FCSTD DOCUMENT  (FreeCAD 0.19R)
Label: EBLclip
License: All rights reserved
LicenseURL: http://en.wikipedia.org/wiki/All_rights_reserved
objects: PartDesign::Chamfer×8, Sketcher::SketchObject×4, PartDesign::Pocket×3, PartDesign::Fillet×2, PartDesign::Pad×1, PartDesign::Body×1, Mesh::Feature×1
note: 33 computed .brp shape members not serialized (recipe doc carries the construction recipe); baked Part::Feature solids carry a one-line shape summary decoded from their .brp

FEATURE [Sketcher::SketchObject] Sketch
  FullyConstrained = true
  MapMode = 5
  Placement = pos=(0,0,0) rot=(1,0,0;1.5708rad)
  Support = -> [XZ_Plane]
  sketch-geometry (8):
    g0: LineSegment StartX=-75 StartY=0 StartZ=0 EndX=-75 EndY=4 EndZ=0
    g1: LineSegment StartX=-75 StartY=4 StartZ=0 EndX=-65 EndY=4 EndZ=0
    g2: LineSegment StartX=-65 StartY=4 StartZ=0 EndX=-65 EndY=30 EndZ=0
    g3: LineSegment StartX=-65 StartY=30 StartZ=0 EndX=65 EndY=30 EndZ=0
    g4: LineSegment StartX=65 StartY=30 StartZ=0 EndX=65 EndY=4 EndZ=0
    g5: LineSegment StartX=65 StartY=4 StartZ=0 EndX=75 EndY=4 EndZ=0
    g6: LineSegment StartX=75 StartY=4 StartZ=0 EndX=75 EndY=0 EndZ=0
    g7: LineSegment StartX=75 StartY=0 StartZ=0 EndX=-75 EndY=0 EndZ=0
  constraints (21):
    c: PointOnObject(g0,g-1)
    c: Coincident(g0,g1)
    c: Horizontal(g1)
    c: Coincident(g2,g3)
    c: Coincident(g3,g4)
    c: Vertical(g4)
    c: Coincident(g5,g6)
    c: Coincident(g7,g0)
    c: Horizontal(g7)
    c: Symmetric(g3,g2,g-2)
    c: Symmetric(g1,g4,g-2)
    c: Coincident(g4,g5)
    c: Vertical(g0)
    c: Vertical(g6)
    c: Symmetric(g0,g5,g-2)
    c: Distance(g6) = 4
    c: Coincident(g2,g1)
    c: Distance(g5) = 10
    c: Coincident(g7,g6)
    c: Distance(g4,g1) = 130
    c: DistanceY(g3) = 30
FEATURE [PartDesign::Pad] Pad
  Direction = (1,1,1)
  Length = 32
  Length2 = 100
  Placement = pos=(0,0,0) rot=(1,0,0;1.5708rad)
  Profile = -> Sketch
  Type = 0
FEATURE [Sketcher::SketchObject] Sketch001
  FullyConstrained = false
  MapMode = 5
  Placement = pos=(0,0,0) rot=(-1,0,0;1.5708rad)
  Support = -> [Pad]
  sketch-geometry (4):
    g0: LineSegment StartX=-62.5 StartY=4.52752 StartZ=0 EndX=62.5 EndY=4.52752 EndZ=0
    g1: LineSegment StartX=62.5 StartY=4.52752 StartZ=0 EndX=62.5 EndY=-28 EndZ=0
    g2: LineSegment StartX=62.5 StartY=-28 StartZ=0 EndX=-62.5 EndY=-28 EndZ=0
    g3: LineSegment StartX=-62.5 StartY=-28 StartZ=0 EndX=-62.5 EndY=4.52752 EndZ=0
  constraints (10):
    c: Coincident(g0,g1)
    c: Coincident(g1,g2)
    c: Coincident(g2,g3)
    c: Coincident(g3,g0)
    c: Horizontal(g2)
    c: Vertical(g1)
    c: Vertical(g3)
    c: DistanceY(g1) = -28
    c: Symmetric(g0,g0,g-2)
    c: Distance(g0) = 125
FEATURE [PartDesign::Pocket] Pocket
  BaseFeature = -> Pad
  Length = 23
  Length2 = 100
  Placement = pos=(0,0,0) rot=(1,0,0;1.5708rad)
  Profile = -> Sketch001
  Type = 0
FEATURE [PartDesign::Fillet] Fillet
  Base = -> Pocket [Edge32,Edge28]
  BaseFeature = -> Pocket
  Placement = pos=(0,0,0) rot=(1,0,0;1.5708rad)
  Radius = 10
  SupportTransform = false
FEATURE [PartDesign::Fillet] Fillet001
  Base = -> Fillet [Edge34,Edge36]
  BaseFeature = -> Fillet
  Placement = pos=(0,0,0) rot=(1,0,0;1.5708rad)
  Radius = 10
  SupportTransform = false
FEATURE [Sketcher::SketchObject] Sketch002
  FullyConstrained = true
  MapMode = 5
  Placement = pos=(0,4.4e-15,4) rot=(0,0,1;3.14159rad)
  Support = -> [Fillet001]
  sketch-geometry (14):
    g0: LineSegment StartX=-68.8453 StartY=14 StartZ=0 EndX=-67.6906 EndY=16 EndZ=0
    g1: LineSegment StartX=-67.6906 StartY=16 StartZ=0 EndX=-68.8453 EndY=18 EndZ=0
    g2: LineSegment StartX=-68.8453 StartY=18 StartZ=0 EndX=-71.1547 EndY=18 EndZ=0
    g3: LineSegment StartX=-71.1547 StartY=18 StartZ=0 EndX=-72.3094 EndY=16 EndZ=0
    g4: LineSegment StartX=-72.3094 StartY=16 StartZ=0 EndX=-71.1547 EndY=14 EndZ=0
    g5: LineSegment StartX=-71.1547 StartY=14 StartZ=0 EndX=-68.8453 EndY=14 EndZ=0
    g6: Circle CenterX=-70 CenterY=16 CenterZ=0 NormalX=0 NormalY=0 NormalZ=1 AngleXU=0 Radius=2.3094
    g7: LineSegment StartX=71.1547 StartY=14 StartZ=0 EndX=72.3094 EndY=16 EndZ=0
    g8: LineSegment StartX=72.3094 StartY=16 StartZ=0 EndX=71.1547 EndY=18 EndZ=0
    g9: LineSegment StartX=71.1547 StartY=18 StartZ=0 EndX=68.8453 EndY=18 EndZ=0
    g10: LineSegment StartX=68.8453 StartY=18 StartZ=0 EndX=67.6906 EndY=16 EndZ=0
    g11: LineSegment StartX=67.6906 StartY=16 StartZ=0 EndX=68.8453 EndY=14 EndZ=0
    g12: LineSegment StartX=68.8453 StartY=14 StartZ=0 EndX=71.1547 EndY=14 EndZ=0
    g13: Circle CenterX=70 CenterY=16 CenterZ=0 NormalX=0 NormalY=0 NormalZ=1 AngleXU=0 Radius=2.3094
  constraints (33):
    c: Coincident(g0,g1)
    c: Coincident(g1,g2)
    c: Coincident(g2,g3)
    c: Coincident(g3,g4)
    c: Coincident(g4,g5)
    c: Coincident(g5,g0)
    c: Equal(g0, g1-g5) x5
    c: PointOnObject(g0,g6)
    c: PointOnObject(g1,g6)
    c: PointOnObject(g2,g6)
    c: PointOnObject(g3,g6)
    c: PointOnObject(g4,g6)
    c: PointOnObject(g5,g6)
    c: Coincident(g7,g8)
    c: Coincident(g8,g9)
    c: Coincident(g9,g10)
    c: Coincident(g10,g11)
    c: Coincident(g11,g12)
    c: Coincident(g12,g7)
    c: Equal(g7, g8-g12) x5
    c: PointOnObject(g7,g13)
    c: PointOnObject(g8,g13)
    c: PointOnObject(g9,g13)
    c: PointOnObject(g10,g13)
    c: PointOnObject(g11,g13)
    c: PointOnObject(g12,g13)
    c: Symmetric(g13,g6,g-2)
    c: Distance(g8,g10) = 4
    c: DistanceY(g13) = 16
    c: DistanceX(g13) = 70
    c: Equal(g9,g2)
    c: Horizontal(g2)
    c: Horizontal(g9)
FEATURE [PartDesign::Pocket] Pocket001
  BaseFeature = -> Fillet001
  Length = 5
  Length2 = 100
  Placement = pos=(0,0,0) rot=(1,0,0;1.5708rad)
  Profile = -> Sketch002
  Type = 0
FEATURE [PartDesign::Chamfer] Chamfer
  Angle = 45
  Base = -> Pocket001 [Edge12,Edge67,Edge5,Edge33]
  BaseFeature = -> Pocket001
  ChamferType = 0
  FlipDirection = false
  Placement = pos=(0,0,0) rot=(1,0,0;1.5708rad)
  Size = 2
  Size2 = 1
  SupportTransform = false
FEATURE [Sketcher::SketchObject] Sketch003
  FullyConstrained = true
  MapMode = 5
  Placement = pos=(-65,0,0) rot=(0.707107,0,-0.707107;3.14159rad)
  Support = -> [Chamfer]
  sketch-geometry (4):
    g0: LineSegment StartX=-12 StartY=12 StartZ=0 EndX=-4 EndY=12 EndZ=0
    g1: LineSegment StartX=-4 StartY=12 StartZ=0 EndX=-4 EndY=0 EndZ=0
    g2: LineSegment StartX=-4 StartY=0 StartZ=0 EndX=-12 EndY=0 EndZ=0
    g3: LineSegment StartX=-12 StartY=0 StartZ=0 EndX=-12 EndY=12 EndZ=0
  constraints (12):
    c: Coincident(g0,g1)
    c: Coincident(g1,g2)
    c: Coincident(g2,g3)
    c: Coincident(g3,g0)
    c: Horizontal(g0)
    c: Horizontal(g2)
    c: Vertical(g1)
    c: Vertical(g3)
    c: Distance(g1) = 12
    c: Distance(g0) = 8
    c: DistanceX(g1) = -4
    c: PointOnObject(g2,g-1)
FEATURE [PartDesign::Pocket] Pocket002
  BaseFeature = -> Chamfer
  Length = 5
  Length2 = 100
  Placement = pos=(0,0,0) rot=(1,0,0;1.5708rad)
  Profile = -> Sketch003
  Type = 0
FEATURE [PartDesign::Chamfer] Chamfer001
  Angle = 45
  Base = -> Pocket002 [Edge67]
  BaseFeature = -> Pocket002
  ChamferType = 0
  FlipDirection = false
  Placement = pos=(0,0,0) rot=(1,0,0;1.5708rad)
  Size = 1
  Size2 = 1
  SupportTransform = false
FEATURE [PartDesign::Chamfer] Chamfer002
  Angle = 45
  Base = -> Chamfer001 [Edge41]
  BaseFeature = -> Chamfer001
  ChamferType = 0
  FlipDirection = false
  Placement = pos=(0,0,0) rot=(1,0,0;1.5708rad)
  Size = 1
  Size2 = 1
  SupportTransform = false
FEATURE [PartDesign::Chamfer] Chamfer003
  Angle = 45
  Base = -> Chamfer002 [Edge34]
  BaseFeature = -> Chamfer002
  ChamferType = 0
  FlipDirection = false
  Placement = pos=(0,0,0) rot=(1,0,0;1.5708rad)
  Size = 4
  Size2 = 1
  SupportTransform = false
FEATURE [PartDesign::Chamfer] Chamfer004
  Angle = 45
  Base = -> Chamfer003 [Edge74]
  BaseFeature = -> Chamfer003
  ChamferType = 0
  FlipDirection = false
  Placement = pos=(0,0,0) rot=(1,0,0;1.5708rad)
  Size = 1
  Size2 = 1
  SupportTransform = false
FEATURE [PartDesign::Chamfer] Chamfer005
  Angle = 45
  Base = -> Chamfer004 [Edge73]
  BaseFeature = -> Chamfer004
  ChamferType = 0
  FlipDirection = false
  Placement = pos=(0,0,0) rot=(1,0,0;1.5708rad)
  Size = 1
  Size2 = 1
  SupportTransform = false
FEATURE [PartDesign::Chamfer] Chamfer006
  Angle = 45
  Base = -> Chamfer005 [Edge38]
  BaseFeature = -> Chamfer005
  ChamferType = 0
  FlipDirection = false
  Placement = pos=(0,0,0) rot=(1,0,0;1.5708rad)
  Size = 1
  Size2 = 1
  SupportTransform = false
FEATURE [PartDesign::Chamfer] Chamfer007
  Angle = 45
  Base = -> Chamfer006 [Edge70]
  BaseFeature = -> Chamfer006
  ChamferType = 0
  FlipDirection = false
  Placement = pos=(0,0,0) rot=(1,0,0;1.5708rad)
  Size = 1
  Size2 = 1
  SupportTransform = false
FEATURE [PartDesign::Body] Body
  Group = -> [Sketch,Pad,Sketch001,Pocket,Fillet,Fillet001,Sketch002,Pocket001,Chamfer,Sketch003,Pocket002,Chamfer001,Chamfer002,Chamfer003,Chamfer004,Chamfer005,Chamfer006,Chamfer007]
  Origin = -> Origin
  Tip = -> Chamfer007
FEATURE [Mesh::Feature] Mesh  label="Chamfer007 (Meshed)"
